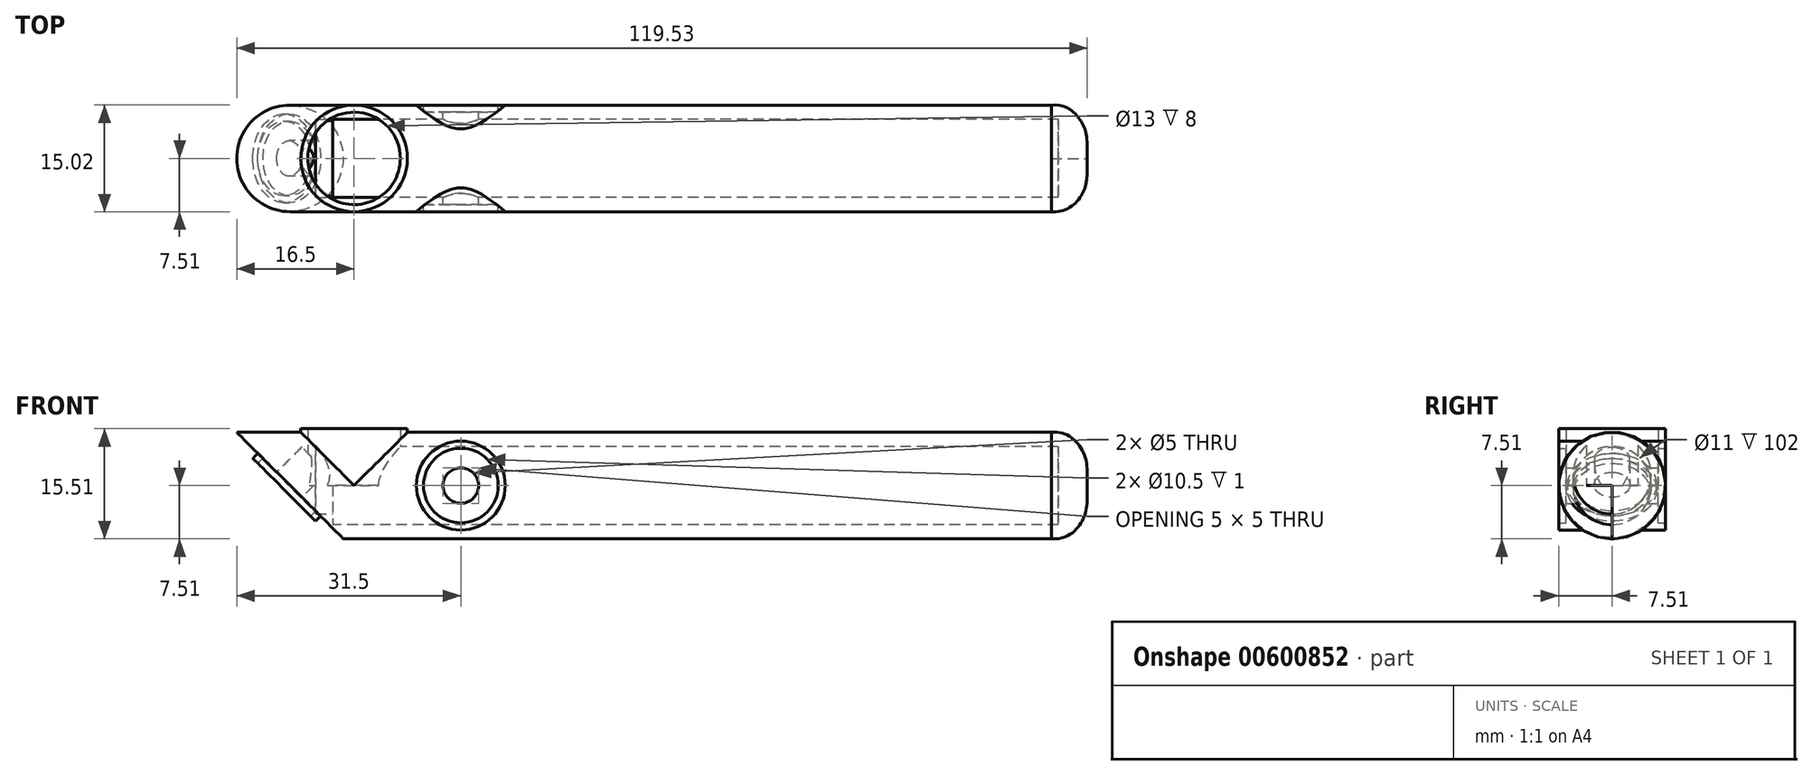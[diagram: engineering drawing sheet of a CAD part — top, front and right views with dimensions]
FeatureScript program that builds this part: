
annotation { "Feature Type Name" : "Feature", "Feature Type Description" : "" }
export const myFeature = defineFeature(function(context is Context, id is Id, definition is map)
    precondition{}
    {
        {
            var Q0;
            Q0=qCreatedBy(makeId("Front.planeOp"),FACE);
            var sketch = newSketch(context, id + "F0", { "sketchPlane" : qUnion([Q0])});
            skLineSegment(sketch, "E0", {"start": v(0, 0) * mm, "end": v(0, -7.5) * mm});
            skLineSegment(sketch, "E1", {"start": v(0, -7.5) * mm, "end": v(115, -7.5) * mm});
            skFitSpline(sketch, "E2", {"points": [v(115, -7.5) * mm, v(119.26, -5.1) * mm, v(120, 0) * mm], "startDerivative": vector(14.27, -1) * mm, "endDerivative": vector(-0.65, 17.78) * mm});
            skLineSegment(sketch, "E3", {"start": v(-3.67, 0) * mm, "end": v(171.97, 0) * mm});
            skSolve(sketch);
        }
        {
            var Q0;
            {var subQ0=sQuery(id+"F0.wireOp",EDGE,"E0");Q0=makeQuery(id+"F0.imprint","IMPRINT",FACE,{"disambiguationData":[TD([[makeQuery(id+"F0.imprint","IMPRINT",EDGE,{"derivedFrom":subQ0}),1.0]])]});}
            var Q1;
            Q1=sQuery(id+"F0.wireOp",EDGE,"E0");
            var Q2;
            Q2=sQuery(id+"F0.wireOp",EDGE,"E1");
            var Q3;
            Q3=sQuery(id+"F0.wireOp",EDGE,"E2");
            var Q4;
            Q4=sQuery(id+"F0.wireOp",EDGE,"E3");
            revolve(context, id + "F1", {"entities" : qUnion([Q0]), "surfaceEntities" : qUnion([Q1, Q2, Q3]), "axis" : qUnion([Q4]), "revolveType" : RevolveType.FULL});
        }
        {
            var Q0;
            Q0=qCreatedBy(makeId("Front.planeOp"),FACE);
            var sketch = newSketch(context, id + "F2", { "sketchPlane" : qUnion([Q0])});
            skCircle(sketch, "E4", {"center": v(32, 0) * mm, "radius": 5.25 * mm});
            skCircle(sketch, "E5.0", {"center": v(32, 0) * mm, "radius": 6.25 * mm});
            skSolve(sketch);
        }
        {
            var Q0;
            Q0 = qSketchRegion(id + "F2", true);
            extrude(context, id + "F3", {"entities" : qUnion([Q0]), "operationType" : NewBodyOperationType.ADD, "endBound" : BoundingType.SYMMETRIC, "depth" : 15 * mm, "offsetDistance" : 25 * mm});
        }
        {
            var Q0;
            Q0=qCreatedBy(makeId("Front.planeOp"),FACE);
            var sketch = newSketch(context, id + "F4", { "sketchPlane" : qUnion([Q0])});
            skCircle(sketch, "E6", {"center": v(32, 0) * mm, "radius": 5.25 * mm});
            skSolve(sketch);
        }
        {
            var Q0;
            Q0 = qSketchRegion(id + "F4", true);
            extrude(context, id + "F5", {"entities" : qUnion([Q0]), "operationType" : NewBodyOperationType.REMOVE, "endBound" : BoundingType.SYMMETRIC, "depth" : 25 * mm, "offsetDistance" : 25 * mm});
        }
        {
            var Q0;
            Q0=qCreatedBy(makeId("Front.planeOp"),FACE);
            var sketch = newSketch(context, id + "F6", { "sketchPlane" : qUnion([Q0])});
            skCircle(sketch, "E7", {"center": v(32, 0) * mm, "radius": 5.25 * mm});
            skSolve(sketch);
        }
        {
            var Q0;
            Q0 = qSketchRegion(id + "F6", true);
            extrude(context, id + "F7", {"entities" : qUnion([Q0]), "operationType" : NewBodyOperationType.ADD, "endBound" : BoundingType.SYMMETRIC, "depth" : 13 * mm, "offsetDistance" : 25 * mm});
        }
        {
            var Q0;
            Q0=qCreatedBy(makeId("Front.planeOp"),FACE);
            var sketch = newSketch(context, id + "F8", { "sketchPlane" : qUnion([Q0])});
            skCircle(sketch, "E8", {"center": v(32, 0) * mm, "radius": 2.5 * mm});
            skSolve(sketch);
        }
        {
            var Q0;
            Q0 = qSketchRegion(id + "F8", true);
            extrude(context, id + "F9", {"entities" : qUnion([Q0]), "operationType" : NewBodyOperationType.REMOVE, "endBound" : BoundingType.SYMMETRIC, "depth" : 25 * mm, "offsetDistance" : 25 * mm});
        }
        {
            var Q0;
            Q0=qCreatedBy(makeId("Top.planeOp"),FACE);
            var sketch = newSketch(context, id + "F10", { "sketchPlane" : qUnion([Q0])});
            skCircle(sketch, "E9", {"center": v(17, 0) * mm, "radius": 6.5 * mm});
            skCircle(sketch, "E10.0", {"center": v(17, 0) * mm, "radius": 7.5 * mm});
            skSolve(sketch);
        }
        {
            var Q0;
            Q0 = qSketchRegion(id + "F10", true);
            extrude(context, id + "F11", {"entities" : qUnion([Q0]), "operationType" : NewBodyOperationType.ADD, "depth" : 8 * mm, "offsetDistance" : 25 * mm});
        }
        {
            var Q0;
            Q0=qCreatedBy(makeId("Top.planeOp"),FACE);
            var sketch = newSketch(context, id + "F12", { "sketchPlane" : qUnion([Q0])});
            skCircle(sketch, "E11", {"center": v(17, 0) * mm, "radius": 6.5 * mm});
            skSolve(sketch);
        }
        {
            var Q0;
            Q0 = qSketchRegion(id + "F12", true);
            extrude(context, id + "F13", {"entities" : qUnion([Q0]), "operationType" : NewBodyOperationType.REMOVE, "depth" : 25 * mm, "offsetDistance" : 25 * mm});
        }
        {
            var Q0;
            Q0=qCreatedBy(makeId("Front.planeOp"),FACE);
            var sketch = newSketch(context, id + "F14", { "sketchPlane" : qUnion([Q0])});
            skLineSegment(sketch, "E12", {"start": v(-3, 11) * mm, "end": v(17, -9) * mm});
            skLineSegment(sketch, "E13", {"start": v(-3, 11) * mm, "end": v(-3, -9) * mm});
            skLineSegment(sketch, "E14", {"start": v(-3, -9) * mm, "end": v(17, -9) * mm});
            skSolve(sketch);
        }
        {
            var Q0;
            Q0 = qSketchRegion(id + "F14", true);
            extrude(context, id + "F15", {"entities" : qUnion([Q0]), "operationType" : NewBodyOperationType.REMOVE, "endBound" : BoundingType.SYMMETRIC, "oppositeDirection" : true, "depth" : 25 * mm, "offsetDistance" : 25 * mm});
        }
        {
            var Q0;
            Q0=qCreatedBy(makeId("Right.planeOp"),FACE);
            cPlane(context, id + "F16", {"entities" : qUnion([Q0]), "cplaneType" : CPlaneType.OFFSET, "offset" : 14 * mm, "width" : 150 * mm, "height" : 150 * mm});
        }
        {
            var Q0;
            Q0=qCreatedBy(id+"F16.planeOp",FACE);
            var sketch = newSketch(context, id + "F17", { "sketchPlane" : qUnion([Q0])});
            skCircle(sketch, "E15", {"center": v(0, 0) * mm, "radius": 5.5 * mm});
            skSolve(sketch);
        }
        {
            var Q0;
            Q0 = qSketchRegion(id + "F17", true);
            extrude(context, id + "F18", {"entities" : qUnion([Q0]), "operationType" : NewBodyOperationType.REMOVE, "depth" : 102 * mm, "offsetDistance" : 25 * mm});
        }
        {
            var Q0;
            Q0=makeQuery(id+"F15.boolean.opBoolean","COPY",FACE,{"derivedFrom":makeQuery(id+"F15.opExtrude","SWEPT_FACE",FACE,{"disambiguationData":[OSD([sQuery(id+"F14.wireOp",EDGE,"E12")])]})});
            cPlane(context, id + "F19", {"entities" : qUnion([Q0]), "cplaneType" : CPlaneType.OFFSET, "offset" : 0 * mm, "width" : 150 * mm, "height" : 150 * mm});
        }
        {
            var Q0;
            Q0=qCreatedBy(id+"F19.planeOp",FACE);
            var sketch = newSketch(context, id + "F20", { "sketchPlane" : qUnion([Q0])});
            skCircle(sketch, "E16", {"center": v(0, -5.5) * mm, "radius": 5.25 * mm});
            skCircle(sketch, "E17.0", {"center": v(0, -5.5) * mm, "radius": 6.25 * mm});
            skSolve(sketch);
        }
        {
            var Q0;
            Q0=makeQuery(id+"F20.imprint","IMPRINT",FACE,{"disambiguationData":[TD([[makeQuery(id+"F20.imprint","IMPRINT",EDGE,{"derivedFrom":sQuery(id+"F20.wireOp",EDGE,"E16")}),-1.0]])]});
            extrude(context, id + "F21", {"entities" : qUnion([Q0]), "operationType" : NewBodyOperationType.ADD, "depth" : 1 * mm, "offsetDistance" : 25 * mm});
        }
        {
            var Q0;
            Q0=qCreatedBy(id+"F16.planeOp",FACE);
            var sketch = newSketch(context, id + "F22", { "sketchPlane" : qUnion([Q0])});
            skCircle(sketch, "E18", {"center": v(0, 1.5) * mm, "radius": 5.5 * mm});
            skSolve(sketch);
        }
        {
            var Q0;
            Q0 = qSketchRegion(id + "F22", true);
            extrude(context, id + "F23", {"entities" : qUnion([Q0]), "operationType" : NewBodyOperationType.REMOVE, "oppositeDirection" : true, "depth" : 2.4 * mm, "offsetDistance" : 25 * mm});
        }
        {
            var Q0;
            Q0=qCreatedBy(id+"F19.planeOp",FACE);
            var sketch = newSketch(context, id + "F24", { "sketchPlane" : qUnion([Q0])});
            skCircle(sketch, "E19", {"center": v(0, -5.5) * mm, "radius": 2.5 * mm});
            skSolve(sketch);
        }
        {
            var Q0;
            Q0 = qSketchRegion(id + "F24", true);
            extrude(context, id + "F25", {"entities" : qUnion([Q0]), "operationType" : NewBodyOperationType.REMOVE, "oppositeDirection" : true, "depth" : 5 * mm, "offsetDistance" : 25 * mm});
        }
    });
